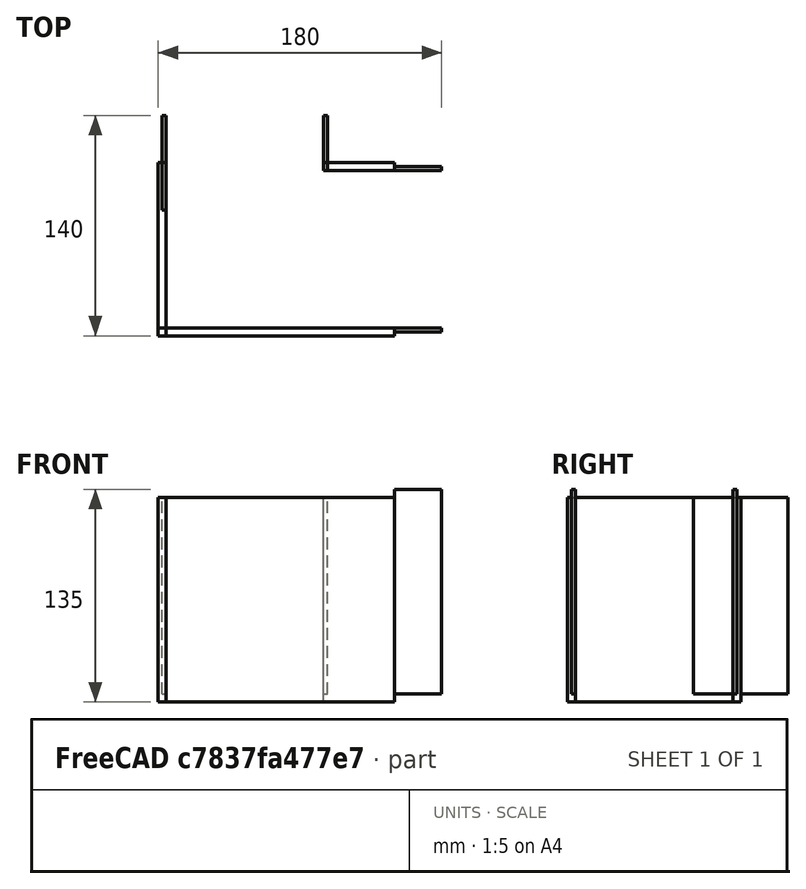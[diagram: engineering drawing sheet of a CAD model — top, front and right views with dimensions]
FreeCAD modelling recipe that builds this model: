
FCSTD DOCUMENT  (FreeCAD 0.19R24291 (Git))
Label: w maze right coner
License: All rights reserved
LicenseURL: http://en.wikipedia.org/wiki/All_rights_reserved
objects: Part::Box×7, App::MeasureDistance×3, Part::Fuse×2
note: 9 computed .brp shape members not serialized (recipe doc carries the construction recipe); baked Part::Feature solids carry a one-line shape summary decoded from their .brp

FEATURE [Part::Box] Box004  label="Cube004"
  AttacherType = Attacher::AttachEngine3D
  Height = 130
  Length = 5
  Width = 110
FEATURE [Part::Box] Box013  label="Cube013"
  AttacherType = Attacher::AttachEngine3D
  Height = 130
  Length = 45
  Placement = pos=(105,105,0) rot=(0,0,1;0rad)
  Width = 5
FEATURE [Part::Box] Box010  label="Cube010"
  AttacherType = Attacher::AttachEngine3D
  Height = 125
  Length = 2.5
  Placement = pos=(105,105,5) rot=(0,0,1;0rad)
  Width = 35
FEATURE [Part::Box] Box009  label="Cube009"
  AttacherType = Attacher::AttachEngine3D
  Height = 125
  Length = 2.5
  Placement = pos=(2.5,80,5) rot=(0,0,1;0rad)
  Width = 60
FEATURE [Part::Box] Box015  label="Cube015"
  AttacherType = Attacher::AttachEngine3D
  Height = 130
  Length = 150
  Width = 5
FEATURE [Part::Fuse] Fusion002
  Base = -> Box004
  Tool = -> Box013
FEATURE [Part::Box] Box007  label="Cube007"
  AttacherType = Attacher::AttachEngine3D
  Height = 130
  Length = 30
  Placement = pos=(210,105,5) rot=(0,0,1;0rad)
  Width = 2.5
FEATURE [Part::Box] Box006  label="Cube006"
  AttacherType = Attacher::AttachEngine3D
  Height = 130
  Length = 30
  Placement = pos=(210,2.5,5) rot=(0,0,1;0rad)
  Width = 2.5
FEATURE [Part::Fuse] Fusion
  Base = -> Box006
  Placement = pos=(-59.9953,-0.0101703,0) rot=(0,0,1;0rad)
  Tool = -> Box007
FEATURE [App::MeasureDistance] Distance  label="Distance: 125.00 mm"
  Distance = 125.004
  P1 = (239,0,130)
  P2 = (240,0,5)
FEATURE [App::MeasureDistance] Distance001  label="Distance: 30.00 mm"
  Distance = 29.9962
  P1 = (2.5,140,130)
  P2 = (2.5,110.004,130)
FEATURE [App::MeasureDistance] Distance002  label="Distance: 150.00 mm"
  Distance = 150
  P1 = (0,0,130)
  P2 = (150,0,130)
